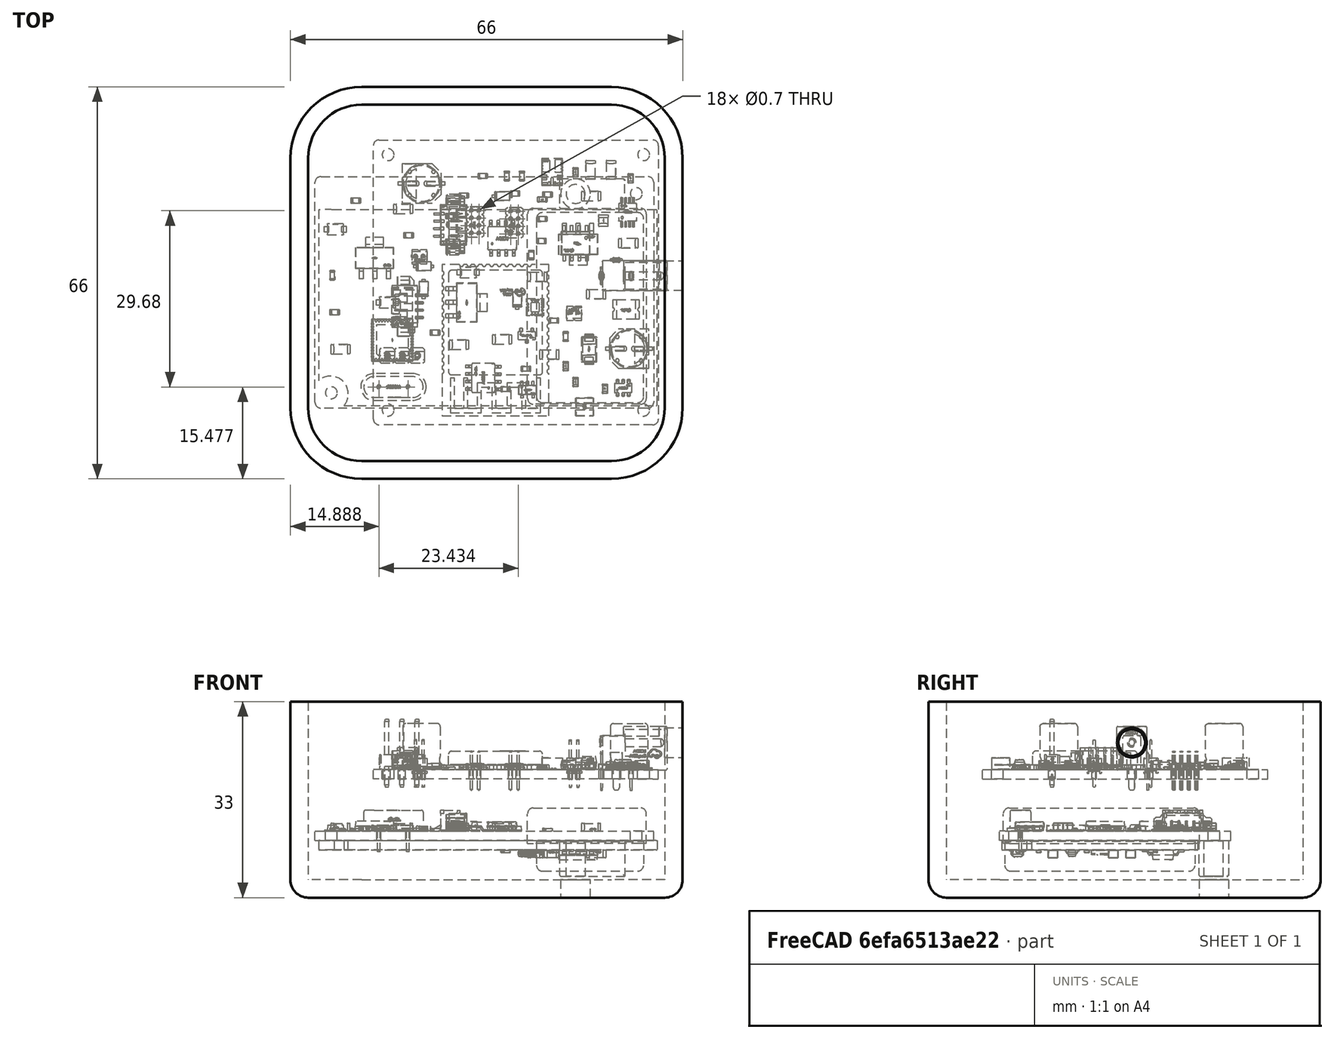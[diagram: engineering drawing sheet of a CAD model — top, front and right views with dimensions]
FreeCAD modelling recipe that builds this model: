
FCSTD DOCUMENT  (FreeCAD 0.21R33771 (Git))
Label: RD_ass
License: All rights reserved
LicenseURL: https://en.wikipedia.org/wiki/All_rights_reserved
objects: Part::FeaturePython×7, Part::Cut×3, PartDesign::ShapeBinder×2, Sketcher::SketchObject×2, Part::Extrusion×2, Part::Cylinder×1, PartDesign::Body×1, App::Part×1
note: 18 computed .brp shape members not serialized (recipe doc carries the construction recipe); baked Part::Feature solids carry a one-line shape summary decoded from their .brp

FEATURE [Part::FeaturePython] b_radar_001_  label="radar_001"  # a2plus imported part (geometry in sourceFile) (typed FeaturePython)
  a2p_Version = 0.4.65
  fixedPosition = true
  objectType = a2pPart
  sourceFile = .\radar.FCStd
  subassemblyImport = false
  timeLastImport = 1.7241e+09
  updateColors = true
FEATURE [Part::FeaturePython] b_scren_top_001_  label="scren_top_001"  # a2plus imported part (geometry in sourceFile) (typed FeaturePython)
  Placement = pos=(45.7639,-21.8345,-0.518072) rot=(0,0,1;1.5708rad)
  a2p_Version = 0.4.65
  fixedPosition = false
  objectType = a2pPart
  sourceFile = .\scren_top.FCStd
  subassemblyImport = false
  timeLastImport = 1.7241e+09
  updateColors = true
FEATURE [Part::FeaturePython] b_Radar_ant_001_  label="Radar_ant_001"  # a2plus imported part (geometry in sourceFile) (typed FeaturePython)
  Placement = pos=(0.583369,-38.5915,-0.00412369) rot=(1,0,0;3.14159rad)
  a2p_Version = 0.4.65
  fixedPosition = false
  objectType = a2pPart
  sourceFile = .\Radar_ant.FCStd
  subassemblyImport = false
  timeLastImport = 1.7241e+09
  updateColors = true
FEATURE [Part::FeaturePython] b_scren_bot_001_  label="scren_bot_001"  # a2plus imported part (geometry in sourceFile) (typed FeaturePython)
  Placement = pos=(46.2874,-22.0715,-0.151866) rot=(1,0,0;3.14159rad)
  a2p_Version = 0.4.65
  fixedPosition = false
  objectType = a2pPart
  sourceFile = .\scren_bot.FCStd
  subassemblyImport = false
  timeLastImport = 1.7241e+09
  updateColors = true
FEATURE [PartDesign::ShapeBinder] Copyb_Radar_ant_001_
  Placement = pos=(0.583369,-38.5915,-0.00412369) rot=(1,0,0;3.14159rad)
  TraceSupport = false
FEATURE [Part::Cylinder] Cylinder  label="Цилиндр"
  Angle = 360
  AttacherType = Attacher::AttachEngine3D
  FirstAngle = 0
  Height = 10
  Placement = pos=(2.6,-36.6,-10) rot=(0,0,1;0rad)
  Radius = 3
  SecondAngle = 0
FEATURE [Part::Cut] Cut
  Base = -> b_Radar_ant_001_
  Tool = -> Cylinder
FEATURE [Part::FeaturePython] b_laser_001_  label="laser_001"  # a2plus imported part (geometry in sourceFile) (typed FeaturePython)
  Placement = pos=(46.6484,-2.91862,-0.0349686) rot=(1,0,0;3.14159rad)
  a2p_Version = 0.4.65
  fixedPosition = false
  objectType = a2pPart
  sourceFile = .\laser.FCStd
  subassemblyImport = false
  timeLastImport = 1.72411e+09
  updateColors = true
FEATURE [Part::FeaturePython] b_shell_001_  label="shell_001"  # a2plus imported part (geometry in sourceFile) (typed FeaturePython)
  Placement = pos=(28.8653,-17.9096,23.381) rot=(0,1,0;3.14159rad)
  a2p_Version = 0.4.65
  fixedPosition = false
  objectType = a2pPart
  sourceFile = .\shell.FCStd
  subassemblyImport = false
  timeLastImport = 1.72411e+09
  updateColors = true
FEATURE [Part::FeaturePython] b_MB1_001_  label="MB1_001"  # a2plus imported part (geometry in sourceFile) (typed FeaturePython)
  Placement = pos=(9.8074,-41.8217,10.3331) rot=(0,0,1;1.5708rad)
  a2p_Version = 0.4.65
  fixedPosition = false
  objectType = a2pPart
  sourceFile = .\MB1.FCStd
  subassemblyImport = false
  timeLastImport = 1.72411e+09
  updateColors = true
FEATURE [Sketcher::SketchObject] Sketch
  FullyConstrained = false
  MapMode = 5
  Placement = pos=(61.8653,-17.9096,23.381) rot=(0.57735,-0.57735,0.57735;4.18879rad)
  Support = -> [b_shell_001_]
  sketch-geometry (1):
    g0: Circle CenterX=-1.22036 CenterY=6.8991 CenterZ=0 NormalX=0 NormalY=0 NormalZ=1 AngleXU=0 Radius=2.5
  constraints (1):
    c: Radius(g0) = 2.5
FEATURE [Part::Extrusion] Extrude
  Base = -> Sketch
  Dir = (1,-2e-16,2e-16)
  DirMode = 2
  FaceMakerClass = Part::FaceMakerBullseye
  LengthFwd = -3
  LengthRev = 0
  Solid = true
  Symmetric = false
FEATURE [Part::Cut] Cut001
  Base = -> b_shell_001_
  Tool = -> Extrude
FEATURE [PartDesign::ShapeBinder] CopyCut001
  Placement = pos=(28.8653,-17.9096,23.381) rot=(0,1,0;3.14159rad)
  TraceSupport = false
FEATURE [PartDesign::Body] Body
  Group = -> [Copyb_Radar_ant_001_,CopyCut001]
  Origin = -> Origin001
FEATURE [App::Part] Part
  Group = -> [Body,Cylinder,b_Radar_ant_001_,Cut]
  Origin = -> Origin
FEATURE [Sketcher::SketchObject] Sketch001
  FullyConstrained = false
  MapMode = 5
  Placement = pos=(0,0,-9.61897) rot=(1,0,0;3.14159rad)
  Support = -> [Cut001]
  sketch-geometry (1):
    g0: Circle CenterX=43.8508 CenterY=2.90594 CenterZ=0 NormalX=0 NormalY=0 NormalZ=1 AngleXU=0 Radius=2.5
  constraints (1):
    c: Radius(g0) = 2.5
FEATURE [Part::Extrusion] Extrude002
  Base = -> Sketch001
  Dir = (1e-16,0,-1)
  DirMode = 2
  FaceMakerClass = Part::FaceMakerBullseye
  LengthFwd = 3
  LengthRev = 0
  Reversed = true
  Solid = true
  Symmetric = false
FEATURE [Part::Cut] Cut002
  Base = -> Cut001
  Tool = -> Extrude002
